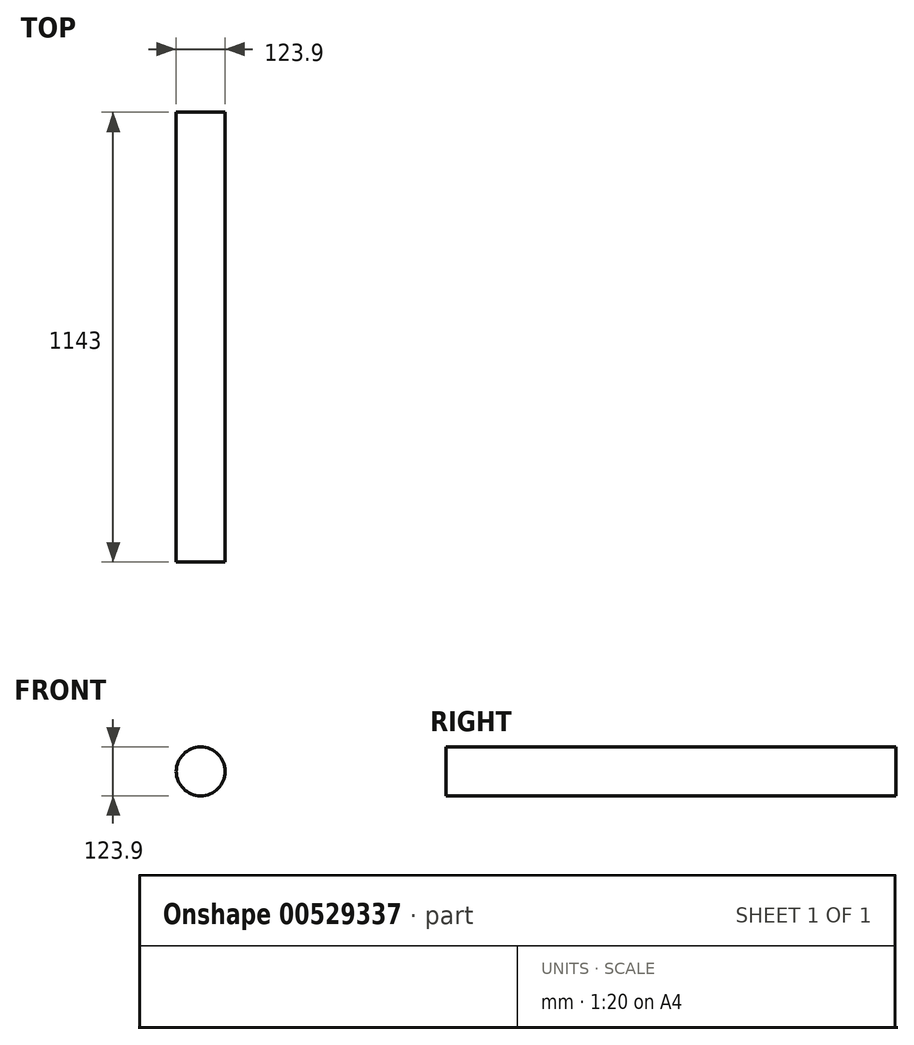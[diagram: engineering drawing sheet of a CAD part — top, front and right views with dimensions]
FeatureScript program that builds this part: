
annotation { "Feature Type Name" : "Feature", "Feature Type Description" : "" }
export const myFeature = defineFeature(function(context is Context, id is Id, definition is map)
    precondition{}
    {
        {
            var Q0;
            Q0=qCreatedBy(makeId("Front.planeOp"),FACE);
            var sketch = newSketch(context, id + "F0", { "sketchPlane" : qUnion([Q0])});
            skCircle(sketch, "E0", {"center": v(0, 0) * mm, "radius": 61.95 * mm});
            skSolve(sketch);
        }
        {
            var Q0;
            Q0=makeQuery(id+"F0.imprint","IMPRINT",FACE,{"disambiguationData":[TD([[makeQuery(id+"F0.imprint","IMPRINT",EDGE,{"derivedFrom":sQuery(id+"F0.wireOp",EDGE,"E0")}),1.0]])]});
            extrude(context, id + "F1", {"entities" : qUnion([Q0]), "depth" : 1143 * mm, "offsetDistance" : 25.4 * mm});
        }
    });
